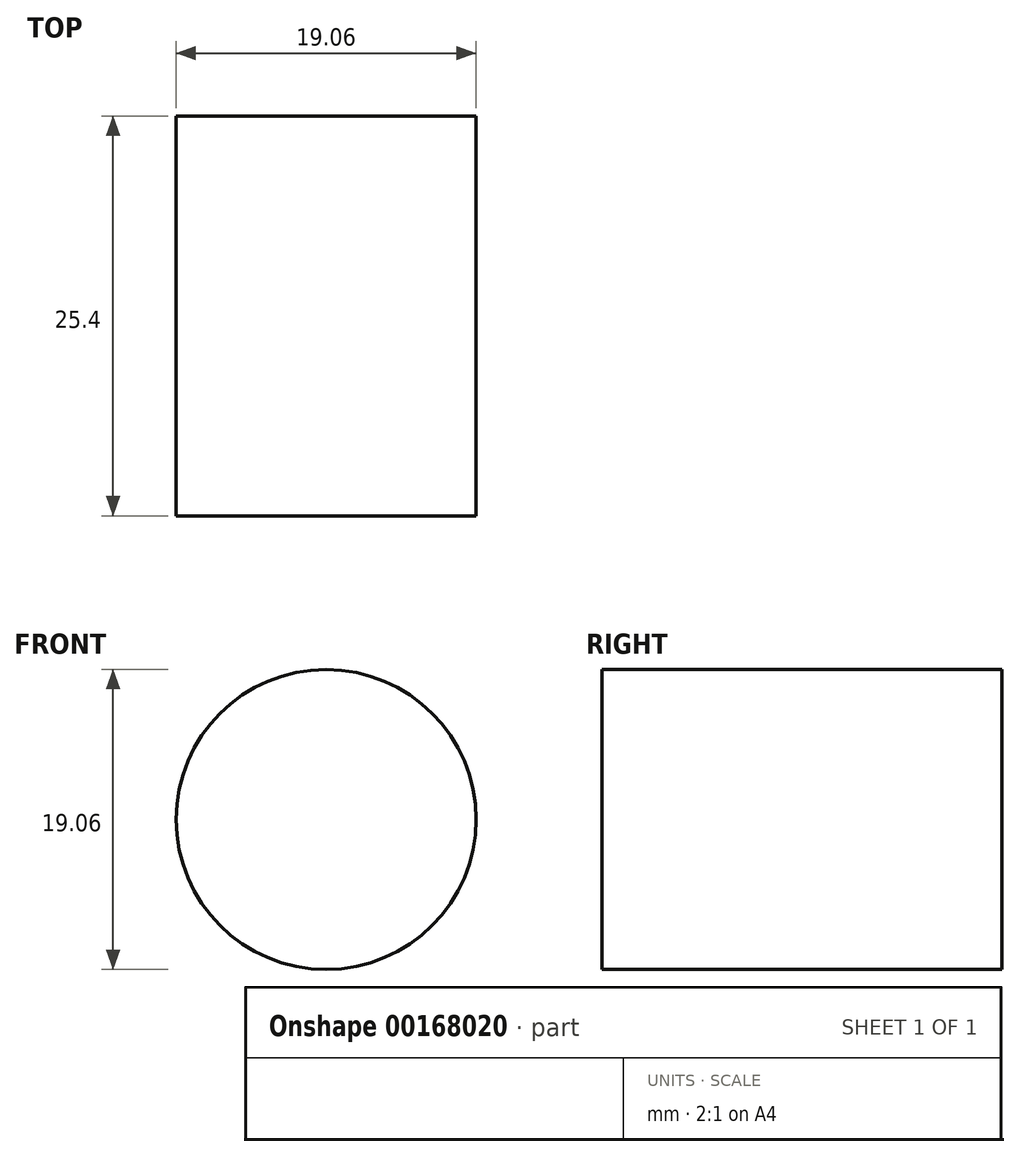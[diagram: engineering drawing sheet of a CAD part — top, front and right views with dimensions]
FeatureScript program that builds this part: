
annotation { "Feature Type Name" : "Feature", "Feature Type Description" : "" }
export const myFeature = defineFeature(function(context is Context, id is Id, definition is map)
    precondition{}
    {
        {
            var Q0;
            Q0=qCreatedBy(makeId("Front.planeOp"),FACE);
            var sketch = newSketch(context, id + "F0", { "sketchPlane" : qUnion([Q0])});
            skCircle(sketch, "E0", {"center": v(0, 0) * mm, "radius": 9.53 * mm});
            skSolve(sketch);
        }
        {
            var Q0;
            Q0 = qSketchRegion(id + "F0", true);
            extrude(context, id + "F1", {"entities" : qUnion([Q0]), "depth" : 25.4 * mm});
        }
        {
            var Q0;
            Q0=qCreatedBy(makeId("Front.planeOp"),FACE);
            var sketch = newSketch(context, id + "F2", { "sketchPlane" : qUnion([Q0])});
            skLineSegment(sketch, "E1.bottom", {"start": v(4.76, -4.76) * mm, "end": v(-4.76, -4.76) * mm});
            skLineSegment(sketch, "E1.top", {"start": v(4.76, 4.76) * mm, "end": v(-4.76, 4.76) * mm});
            skLineSegment(sketch, "E1.left", {"start": v(4.76, -4.76) * mm, "end": v(4.76, 4.76) * mm});
            skLineSegment(sketch, "E1.right", {"start": v(-4.76, -4.76) * mm, "end": v(-4.76, 4.76) * mm});
            skPoint(sketch, "E1.middle", {"position": v(0, 0) * mm});
            skCircle(sketch, "E2", {"center": v(0, 0) * mm, "radius": 4.76 * mm});
            skSolve(sketch);
        }
        {
            var Q0;
            Q0=qCreatedBy(makeId("Front.planeOp"),FACE);
            var sketch = newSketch(context, id + "F3", { "sketchPlane" : qUnion([Q0])});
            skCircle(sketch, "E3.cCircle", {"center": v(0, 0) * mm, "radius": 5.47 * mm, "construction": true});
            skLineSegment(sketch, "E3.0", {"start": v(5.46, -3.18) * mm, "end": v(-0.02, -6.32) * mm});
            skLineSegment(sketch, "E3.1", {"start": v(-0.02, -6.32) * mm, "end": v(-5.49, -3.14) * mm});
            skLineSegment(sketch, "E3.2", {"start": v(-5.49, -3.14) * mm, "end": v(-5.46, 3.18) * mm});
            skLineSegment(sketch, "E3.3", {"start": v(-5.46, 3.18) * mm, "end": v(0.02, 6.32) * mm});
            skLineSegment(sketch, "E3.4", {"start": v(0.02, 6.32) * mm, "end": v(5.49, 3.14) * mm});
            skLineSegment(sketch, "E3.5", {"start": v(5.49, 3.14) * mm, "end": v(5.46, -3.18) * mm});
            skPoint(sketch, "E3.0.midPoint", {"position": v(2.72, -4.75) * mm});
            skSolve(sketch);
        }
        {
            var Q0;
            Q0=makeQuery(id+"F3.imprint","IMPRINT",FACE,{"disambiguationData":[TD([[makeQuery(id+"F3.imprint","IMPRINT",EDGE,{"derivedFrom":sQuery(id+"F3.wireOp",EDGE,"E3.0")}),-1.0]])]});
            extrude(context, id + "F4", {"entities" : qUnion([Q0]), "operationType" : NewBodyOperationType.ADD, "depth" : 25.4 * mm});
        }
    });
